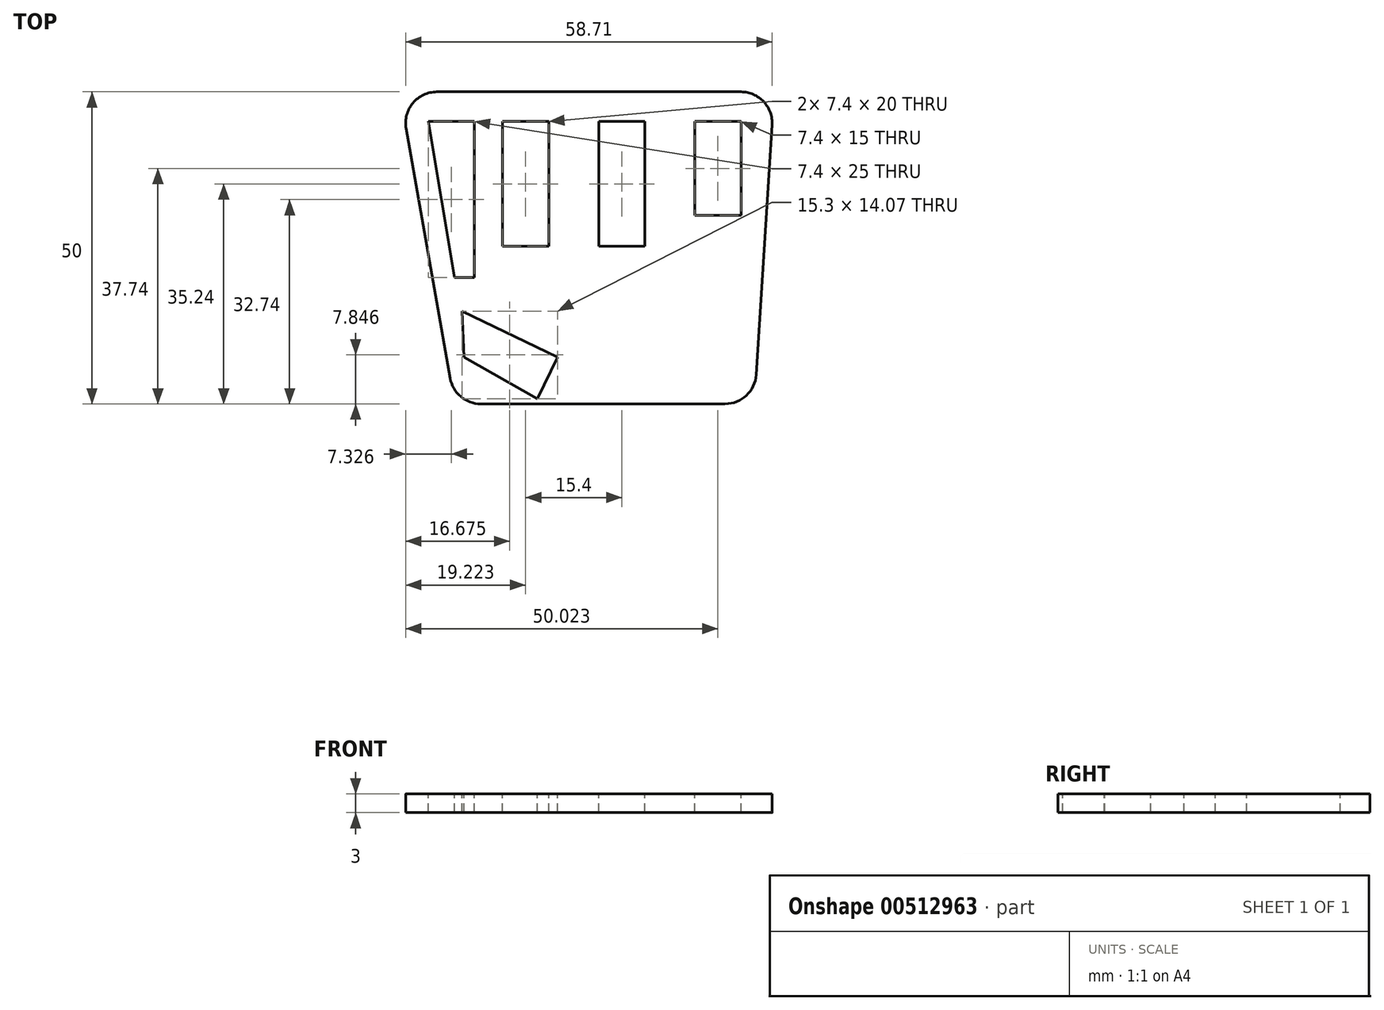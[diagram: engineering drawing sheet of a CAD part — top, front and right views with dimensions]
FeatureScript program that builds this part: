
annotation { "Feature Type Name" : "Feature", "Feature Type Description" : "" }
export const myFeature = defineFeature(function(context is Context, id is Id, definition is map)
    precondition{}
    {
        {
            var Q0;
            Q0=qCreatedBy(makeId("Top.planeOp"),FACE);
            var sketch = newSketch(context, id + "F0", { "sketchPlane" : qUnion([Q0])});
            skLineSegment(sketch, "E0", {"start": v(39.65, 4.76) * mm, "end": v(-20.35, 4.76) * mm});
            skLineSegment(sketch, "E1", {"start": v(-11.53, -45.24) * mm, "end": v(36.47, -45.24) * mm});
            skLineSegment(sketch, "E2", {"start": v(36.47, -45.24) * mm, "end": v(39.65, 4.76) * mm});
            skLineSegment(sketch, "E3", {"start": v(-20.35, 4.76) * mm, "end": v(-11.53, -45.24) * mm});
            skSolve(sketch);
        }
        {
            var Q0;
            Q0=makeQuery(id+"F0.imprint","IMPRINT",FACE,{"disambiguationData":[TD([[makeQuery(id+"F0.imprint","IMPRINT",EDGE,{"derivedFrom":sQuery(id+"F0.wireOp",EDGE,"E0")}),1.0]])]});
            extrude(context, id + "F1", {"entities" : qUnion([Q0]), "depth" : 3 * mm, "offsetDistance" : 25 * mm});
        }
        {
            var Q0;
            Q0=makeQuery(id+"F1.opExtrude","CAP_FACE",FACE,{"disambiguationData":[OSD([sQuery(id+"F0.wireOp",EDGE,"E0"),sQuery(id+"F0.wireOp",EDGE,"E1"),sQuery(id+"F0.wireOp",EDGE,"E2"),sQuery(id+"F0.wireOp",EDGE,"E3")])],"isStart":false});
            var sketch = newSketch(context, id + "F2", { "sketchPlane" : qUnion([Q0])});
            skLineSegment(sketch, "E4.bottom", {"start": v(34.33, 0) * mm, "end": v(26.93, 0) * mm});
            skLineSegment(sketch, "E4.top", {"start": v(34.33, -15) * mm, "end": v(26.93, -15) * mm});
            skLineSegment(sketch, "E4.left", {"start": v(34.33, 0) * mm, "end": v(34.33, -15) * mm});
            skLineSegment(sketch, "E4.right", {"start": v(26.93, 0) * mm, "end": v(26.93, -15) * mm});
            skLineSegment(sketch, "E5.bottom", {"start": v(18.93, 0) * mm, "end": v(11.53, 0) * mm});
            skLineSegment(sketch, "E5.top", {"start": v(18.93, -20) * mm, "end": v(11.53, -20) * mm});
            skLineSegment(sketch, "E5.left", {"start": v(18.93, 0) * mm, "end": v(18.93, -20) * mm});
            skLineSegment(sketch, "E5.right", {"start": v(11.53, 0) * mm, "end": v(11.53, -20) * mm});
            skLineSegment(sketch, "E6.bottom", {"start": v(3.53, 0) * mm, "end": v(-3.87, 0) * mm});
            skLineSegment(sketch, "E6.top", {"start": v(3.53, -20) * mm, "end": v(-3.87, -20) * mm});
            skLineSegment(sketch, "E6.left", {"start": v(3.53, 0) * mm, "end": v(3.53, -20) * mm});
            skLineSegment(sketch, "E6.right", {"start": v(-3.87, 0) * mm, "end": v(-3.87, -20) * mm});
            skLineSegment(sketch, "E7", {"start": v(-15.76, 0) * mm, "end": v(-8.36, 0) * mm});
            skLineSegment(sketch, "E8", {"start": v(-8.36, 0) * mm, "end": v(-8.36, -25) * mm});
            skLineSegment(sketch, "E9", {"start": v(-8.36, -25) * mm, "end": v(-11.53, -25) * mm});
            skLineSegment(sketch, "E10", {"start": v(-11.53, -25) * mm, "end": v(-15.76, 0) * mm});
            skSolve(sketch);
        }
        {
            var Q0;
            Q0 = qSketchRegion(id + "F2", true);
            extrude(context, id + "F3", {"entities" : qUnion([Q0]), "operationType" : NewBodyOperationType.REMOVE, "endBound" : BoundingType.UP_TO_NEXT, "oppositeDirection" : true, "depth" : 25 * mm, "offsetDistance" : 25 * mm});
        }
        {
            var Q0;
            Q0=makeQuery(id+"F1.opExtrude","CAP_FACE",FACE,{"disambiguationData":[OSD([sQuery(id+"F0.wireOp",EDGE,"E0"),sQuery(id+"F0.wireOp",EDGE,"E1"),sQuery(id+"F0.wireOp",EDGE,"E2"),sQuery(id+"F0.wireOp",EDGE,"E3")])],"isStart":false});
            var sketch = newSketch(context, id + "F4", { "sketchPlane" : qUnion([Q0])});
            skLineSegment(sketch, "E11", {"start": v(-10.36, -30.36) * mm, "end": v(4.93, -37.77) * mm});
            skLineSegment(sketch, "E12", {"start": v(4.93, -37.77) * mm, "end": v(1.7, -44.43) * mm});
            skLineSegment(sketch, "E13", {"start": v(1.7, -44.43) * mm, "end": v(-10.06, -37.75) * mm});
            skLineSegment(sketch, "E14", {"start": v(-10.06, -37.75) * mm, "end": v(-10.36, -30.36) * mm});
            skSolve(sketch);
        }
        {
            var Q0;
            Q0=makeQuery(id+"F4.imprint","IMPRINT",FACE,{"disambiguationData":[TD([[makeQuery(id+"F4.imprint","IMPRINT",EDGE,{"derivedFrom":sQuery(id+"F4.wireOp",EDGE,"E11")}),-1.0]])]});
            extrude(context, id + "F5", {"entities" : qUnion([Q0]), "operationType" : NewBodyOperationType.REMOVE, "endBound" : BoundingType.UP_TO_NEXT, "oppositeDirection" : true, "depth" : 25 * mm, "offsetDistance" : 25 * mm});
        }
        {
            var Q0;
            Q0=makeQuery(id+"F1.opExtrude","SWEPT_EDGE",EDGE,{"disambiguationData":[OSD([sQuery(id+"F0.wireOp",EDGE,"E0"),sQuery(id+"F0.wireOp",EDGE,"E3")])]});
            var Q1;
            Q1=makeQuery(id+"F1.opExtrude","SWEPT_EDGE",EDGE,{"disambiguationData":[OSD([sQuery(id+"F0.wireOp",EDGE,"E0"),sQuery(id+"F0.wireOp",EDGE,"E2")])]});
            var Q2;
            Q2=makeQuery(id+"F1.opExtrude","SWEPT_EDGE",EDGE,{"disambiguationData":[OSD([sQuery(id+"F0.wireOp",EDGE,"E1"),sQuery(id+"F0.wireOp",EDGE,"E2")])]});
            var Q3;
            Q3=makeQuery(id+"F1.opExtrude","SWEPT_EDGE",EDGE,{"disambiguationData":[OSD([sQuery(id+"F0.wireOp",EDGE,"E1"),sQuery(id+"F0.wireOp",EDGE,"E3")])]});
            fillet(context, id + "F6", {"entities" : qUnion([Q0, Q1, Q2, Q3]), "radius" : 5 * mm, "tangentPropagation" : true, "allowEdgeOverflow" : false});
        }
    });
